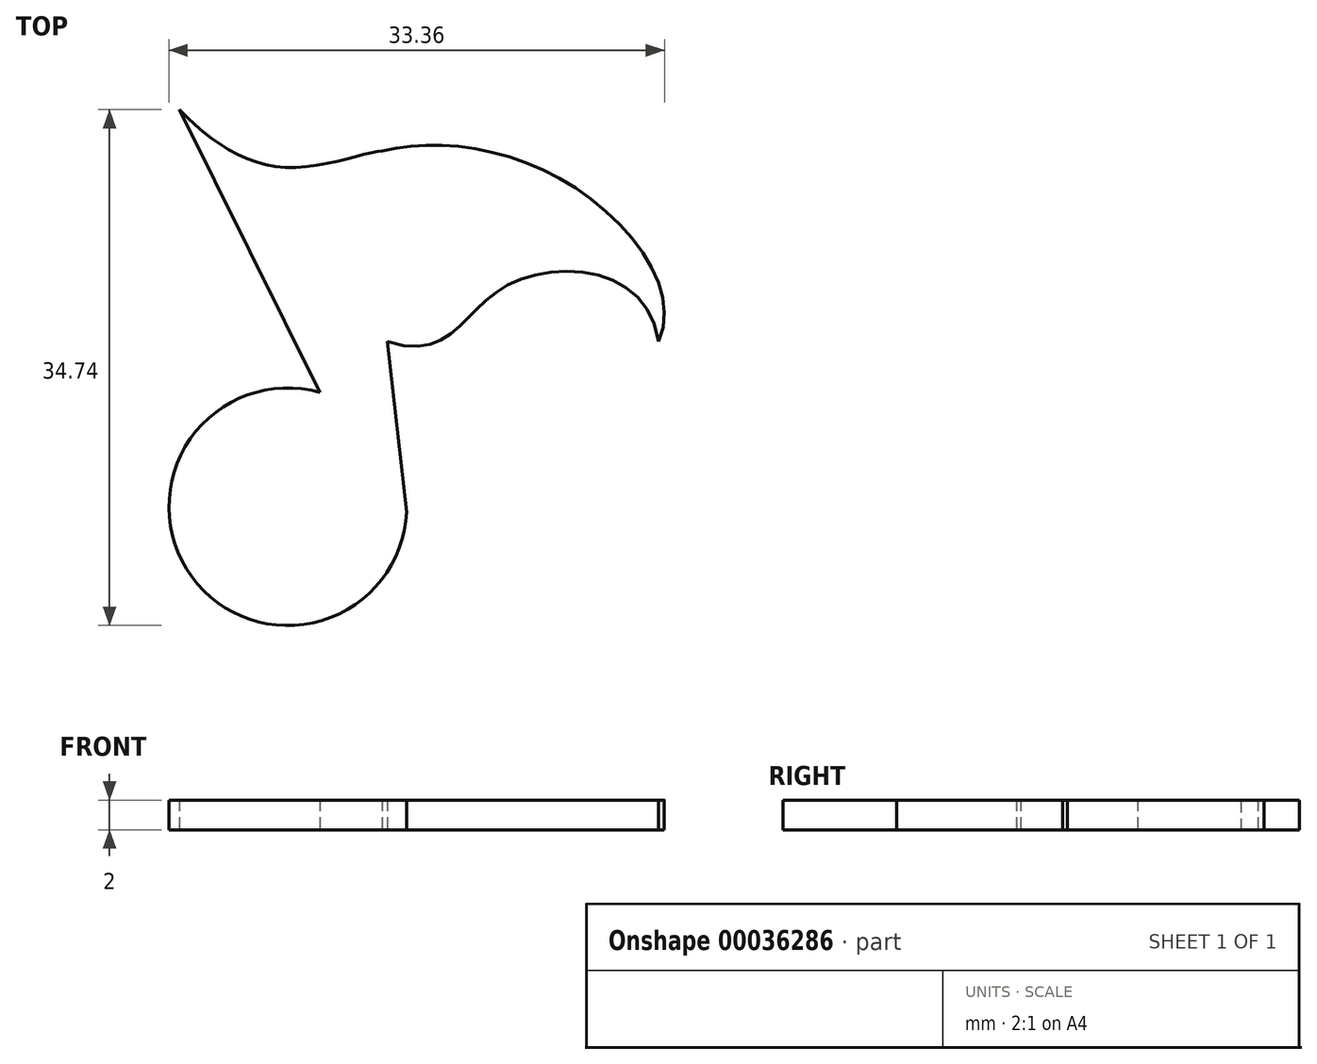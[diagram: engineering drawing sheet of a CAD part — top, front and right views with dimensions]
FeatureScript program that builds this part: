
annotation { "Feature Type Name" : "Feature", "Feature Type Description" : "" }
export const myFeature = defineFeature(function(context is Context, id is Id, definition is map)
    precondition{}
    {
        {
            var Q0;
            Q0=qCreatedBy(makeId("Top.planeOp"),FACE);
            var sketch = newSketch(context, id + "F0", { "sketchPlane" : qUnion([Q0])});
            skArc(sketch, "E0", {"start": v(-3.98, -5.51) * mm, "mid": v(-12.63, -17.9) * mm, "end": v(1.85, -13.56) * mm});
            skLineSegment(sketch, "E1", {"start": v(0.57, -2.1) * mm, "end": v(1.85, -13.56) * mm});
            skLineSegment(sketch, "E2", {"start": v(-3.98, -5.51) * mm, "end": v(-13.43, 13.53) * mm});
            skFitSpline(sketch, "E3", {"points": [v(0.22, 10.75) * mm, v(12.86, 8.49) * mm, v(18.82, -2.1) * mm], "startDerivative": vector(20.74, 5.18) * mm, "endDerivative": vector(-9.53, -21.5) * mm});
            skFitSpline(sketch, "E4", {"points": [v(-13.43, 13.53) * mm, v(-6.15, 9.64) * mm, v(0.22, 10.75) * mm], "startDerivative": vector(11.68, -12.14) * mm, "endDerivative": vector(6.82, 0.29) * mm});
            skFitSpline(sketch, "E5", {"points": [v(0.57, -2.1) * mm, v(8.58, 1.67) * mm, v(18.82, -2.1) * mm], "startDerivative": vector(27.47, -8.8) * mm, "endDerivative": vector(3.96, -29.24) * mm});
            skSolve(sketch);
        }
        {
            var Q0;
            Q0=makeQuery(id+"F0.imprint","IMPRINT",FACE,{"disambiguationData":[TD([[makeQuery(id+"F0.imprint","IMPRINT",EDGE,{"derivedFrom":sQuery(id+"F0.wireOp",EDGE,"E0")}),1.0]])]});
            extrude(context, id + "F1", {"entities" : qUnion([Q0]), "depth" : 2 * mm});
        }
    });
